# Revit family: Faucet-Kitchen-STERLING-Valton-24277_1
name_source: partatom
category: Plumbing Fixtures
units: mm (PartAtom-declared; Revit-internal decimal feet)

## family parameters
Cut with Voids When Loaded = No
Host = Face
OmniClass Number = 23.31.11.00
OmniClass Title = Faucets
Part Type = Normal
Room Calculation Point = No
Round Connector Dimension = Use Diameter
Shared = No

## types (4) — shared parameters
ADA Compliant = Yes
Assembly Code = D2010
CW Connection = Yes
Cold Water Inlet = Cold Water Inlet
Date Modified = 10/11/2022
Default Elevation = 36"
Description = Pull-out single-handle kitchen faucet
Drain Included = No
Flow Rate = 2 GPM
HW Connection = Yes
Handle Clearance = 3 7/16"
Hot Water Inlet = Hot Water Inlet
Length = 9 1/8"
Manufacturer = Sterling Co.
Master Format 2014 = 22 41 39
Master Format 2014 Name = Residential Faucets, Supplies, and Trim
Material = Premium Metal Construction
Pressure = 60.00 psi
Product Documentation Link = https://resources.kohler.com
Product Name = Valton
Product Page URL = http://www.sterlingplumbing.com
Spout Reach = 9 1/8"
URL = https://www.sterlingplumbing.com
Vent Connection = No
Waste Connection = No
Waste Water Outlet = Waste Water Outlet
WaterSense Certified = No

## per-type parameters (varying)
| type | Finish | Model | Type |
| CP-Polished Chrome | Sterling-Metal-CP-Polished_Chrome | 24277-CP | 1 |
| BN-Vibrant Brushed Nickel | Sterling-Metal-BN-Vibrant_Brushed_Nickel | 24277-BN | 3 |
| BL-Matte Black | Sterling-Metal-BL-Matte_Black | 24277-BL | 2 |
| VS-Vibrant Stainless | Sterling-Metal-VS-Vibrant_Stainless | 24277-VS | 4 |

## geometry (parser evidence)
native form markers: Sweep x8
no freeform markers — native parametric forms only
